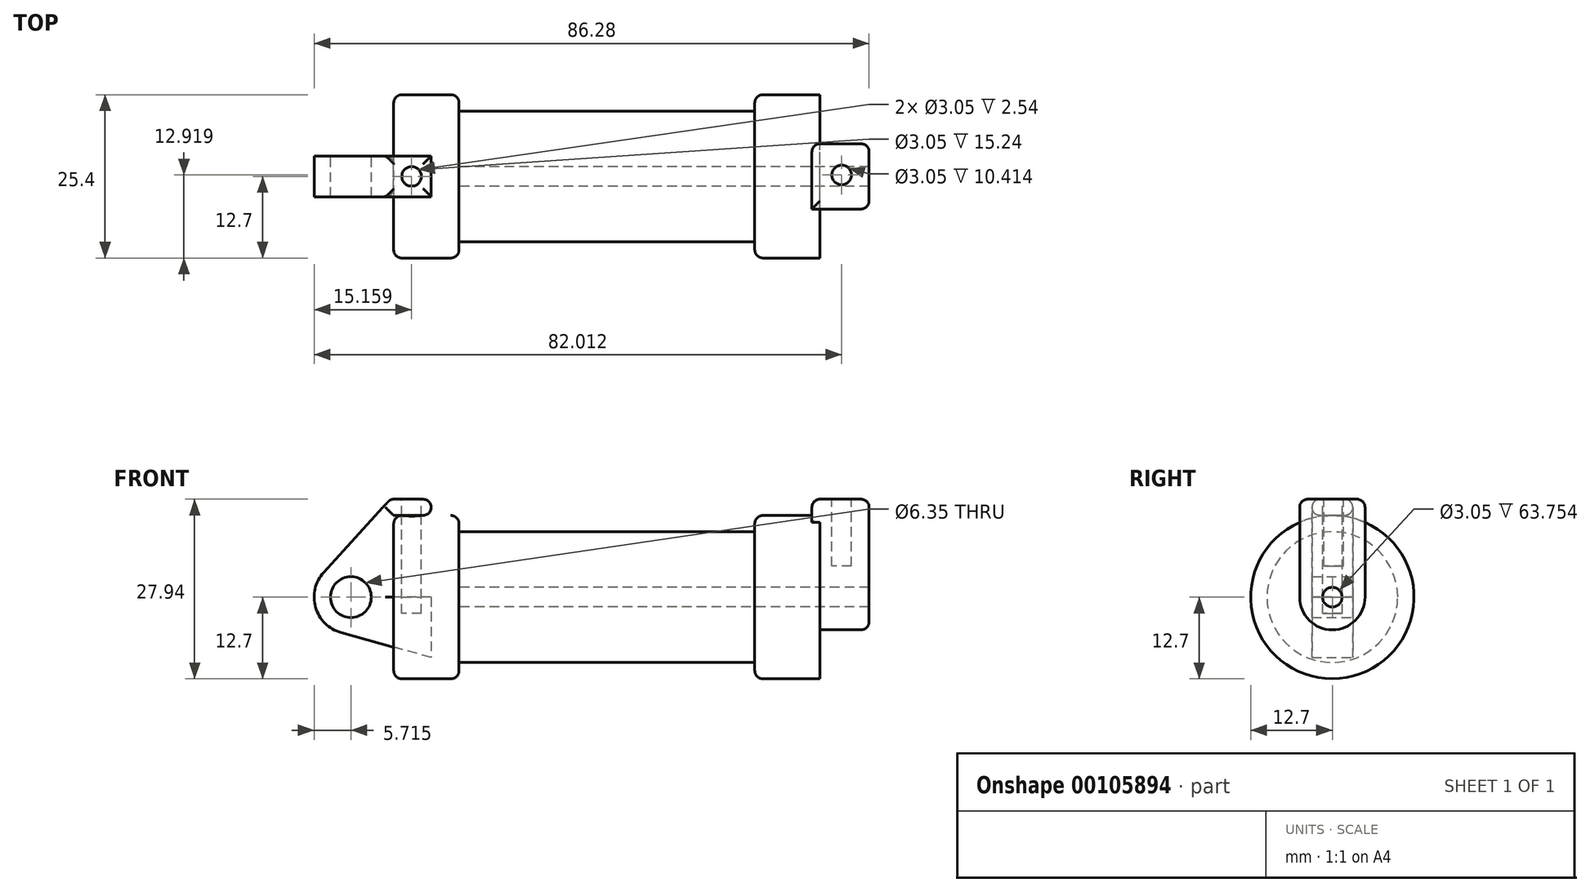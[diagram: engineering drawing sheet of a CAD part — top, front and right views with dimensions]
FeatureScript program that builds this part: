
annotation { "Feature Type Name" : "Feature", "Feature Type Description" : "" }
export const myFeature = defineFeature(function(context is Context, id is Id, definition is map)
    precondition{}
    {
        {
            var Q0;
            Q0=qCreatedBy(makeId("Front.planeOp"),FACE);
            var sketch = newSketch(context, id + "F0", { "sketchPlane" : qUnion([Q0])});
            skLineSegment(sketch, "E0", {"start": v(0, 0) * mm, "end": v(0, 12.7) * mm});
            skLineSegment(sketch, "E1", {"start": v(0, 12.7) * mm, "end": v(10.16, 12.7) * mm});
            skLineSegment(sketch, "E2", {"start": v(10.16, 12.7) * mm, "end": v(10.16, 10.16) * mm});
            skLineSegment(sketch, "E3", {"start": v(10.16, 10.16) * mm, "end": v(56.13, 10.16) * mm});
            skLineSegment(sketch, "E4", {"start": v(56.13, 10.16) * mm, "end": v(56.13, 12.7) * mm});
            skLineSegment(sketch, "E5", {"start": v(56.13, 12.7) * mm, "end": v(66.3, 12.7) * mm});
            skLineSegment(sketch, "E6", {"start": v(66.3, 12.7) * mm, "end": v(66.3, 0) * mm});
            skLineSegment(sketch, "E7", {"start": v(66.3, 0) * mm, "end": v(0, 0) * mm});
            skLineSegment(sketch, "E8", {"start": v(5.84, 15.24) * mm, "end": v(-0.5, 15.24) * mm});
            skLineSegment(sketch, "E9", {"start": v(-0.5, 15.24) * mm, "end": v(-10.88, 3.85) * mm});
            skLineSegment(sketch, "E10", {"start": v(0, 0) * mm, "end": v(-6.65, 0) * mm});
            skCircle(sketch, "E11", {"center": v(-6.65, 0) * mm, "radius": 5.72 * mm});
            skCircle(sketch, "E12", {"center": v(-6.65, 0) * mm, "radius": 3.18 * mm});
            skLineSegment(sketch, "E13", {"start": v(5.84, 15.24) * mm, "end": v(5.84, -9.4) * mm});
            skLineSegment(sketch, "E14", {"start": v(5.84, -9.4) * mm, "end": v(-8.18, -5.5) * mm});
            skSolve(sketch);
        }
        {
            var Q0;
            {var subQ0=sQuery(id+"F0.wireOp",EDGE,"E2");Q0=makeQuery(id+"F0.imprint","IMPRINT",FACE,{"disambiguationData":[TD([[makeQuery(id+"F0.imprint","IMPRINT",EDGE,{"derivedFrom":subQ0}),-1.0]])]});}
            var Q1;
            {var subQ0=sQuery(id+"F0.wireOp",EDGE,"E0");Q1=makeQuery(id+"F0.imprint","IMPRINT",FACE,{"disambiguationData":[TD([[makeQuery(id+"F0.imprint","IMPRINT",EDGE,{"derivedFrom":subQ0}),-1.0]])]});}
            var Q2;
            Q2=sQuery(id+"F0.wireOp",EDGE,"E7");
            revolve(context, id + "F1", {"entities" : qUnion([Q0, Q1]), "axis" : qUnion([Q2]), "revolveType" : RevolveType.FULL});
        }
        {
            var Q0;
            Q0=makeQuery(id+"F1.opRevolve","SWEPT_FACE",FACE,{"disambiguationData":[OSD([sQuery(id+"F0.wireOp",EDGE,"E6")])]});
            var sketch = newSketch(context, id + "F2", { "sketchPlane" : qUnion([Q0])});
            skCircle(sketch, "E15", {"center": v(0, 0) * mm, "radius": 5.08 * mm});
            skCircle(sketch, "E16", {"center": v(0, 0) * mm, "radius": 1.52 * mm});
            skLineSegment(sketch, "E17", {"start": v(-5.08, 0) * mm, "end": v(-5.08, 15.24) * mm});
            skLineSegment(sketch, "E18", {"start": v(5.08, 0) * mm, "end": v(5.08, 15.24) * mm});
            skLineSegment(sketch, "E19", {"start": v(-5.08, 15.24) * mm, "end": v(5.08, 15.24) * mm});
            skLineSegment(sketch, "E20", {"start": v(-2.03, 12.54) * mm, "end": v(-2.03, 15.24) * mm});
            skLineSegment(sketch, "E21", {"start": v(-2.03, 15.24) * mm, "end": v(2.07, 15.24) * mm});
            skLineSegment(sketch, "E22", {"start": v(2.07, 15.24) * mm, "end": v(2.07, 12.53) * mm});
            skSolve(sketch);
        }
        {
            var Q0;
            {var subQ4=sQuery(id+"F0.wireOp",EDGE,"E12");Q0=makeQuery(id+"F0.imprint","IMPRINT",FACE,{"disambiguationData":[TD([[makeQuery(id+"F0.imprint","IMPRINT",EDGE,{"derivedFrom":subQ4}),-1.0]])]});}
            var Q1;
            {var subQ0=sQuery(id+"F0.wireOp",EDGE,"E14");Q1=makeQuery(id+"F0.imprint","IMPRINT",FACE,{"disambiguationData":[TD([[makeQuery(id+"F0.imprint","IMPRINT",EDGE,{"derivedFrom":subQ0}),-1.0]])]});}
            var Q2;
            {var subQ3=sQuery(id+"F0.wireOp",EDGE,"E0");Q2=makeQuery(id+"F0.imprint","IMPRINT",FACE,{"disambiguationData":[TD([[makeQuery(id+"F0.imprint","IMPRINT",EDGE,{"derivedFrom":subQ3}),1.0]])]});}
            extrude(context, id + "F3", {"entities" : qUnion([Q0, Q1, Q2]), "endBound" : BoundingType.SYMMETRIC, "depth" : 6.35 * mm});
        }
        {
            var Q0;
            Q0 = qSketchRegion(id + "F2", true);
            extrude(context, id + "F4", {"entities" : qUnion([Q0]), "operationType" : NewBodyOperationType.ADD, "depth" : 7.62 * mm});
        }
        {
            var Q0;
            Q0=makeQuery(id+"F4.opExtrude","CAP_FACE",FACE,{"disambiguationData":[OSD([sQuery(id+"F2.wireOp",EDGE,"E15"),sQuery(id+"F2.wireOp",EDGE,"E16"),sQuery(id+"F2.wireOp",EDGE,"E17"),sQuery(id+"F2.wireOp",EDGE,"E18"),sQuery(id+"F2.wireOp",EDGE,"E19"),sQuery(id+"F2.wireOp",EDGE,"E21")])],"isStart":true});
            extrude(context, id + "F5", {"entities" : qUnion([Q0]), "operationType" : NewBodyOperationType.ADD, "depth" : 1.27 * mm});
        }
        {
            var Q0;
            Q0=makeQuery(id+"F4.boolean.opBoolean","SPLIT",FACE,{"disambiguationData":[TD([makeQuery(id+"F4.opExtrude","SWEPT_FACE",FACE,{"disambiguationData":[OSD([sQuery(id+"F2.wireOp",EDGE,"E16")])]})])],"derivedFrom":makeQuery(id+"F1.opRevolve","SWEPT_FACE",FACE,{"disambiguationData":[OSD([sQuery(id+"F0.wireOp",EDGE,"E6")])]})});
            var Q1;
            Q1=makeQuery(id+"F1.opRevolve","SWEPT_FACE",FACE,{"disambiguationData":[OSD([sQuery(id+"F0.wireOp",EDGE,"E2")])]});
            extrude(context, id + "F6", {"entities" : qUnion([Q0]), "operationType" : NewBodyOperationType.REMOVE, "endBound" : BoundingType.UP_TO_SURFACE, "oppositeDirection" : true, "endBoundEntityFace" : qUnion([Q1]), "depth" : 25.4 * mm});
        }
        {
            var Q0;
            {var subQ0=sQuery(id+"F2.wireOp",EDGE,"E21");var subQ1=sQuery(id+"F2.wireOp",EDGE,"E19");Q0=makeQuery(id+"F5.boolean.opBoolean","MERGE",FACE,{"derivedFrom":[makeQuery(id+"F4.opExtrude","SWEPT_FACE",FACE,{"disambiguationData":[OSD([subQ1,subQ0])]}),makeQuery(id+"F5.opExtrude","SWEPT_FACE",FACE,{"disambiguationData":[OSD([subQ1,subQ0])]})]});}
            var sketch = newSketch(context, id + "F7", { "sketchPlane" : qUnion([Q0])});
            skCircle(sketch, "E23", {"center": v(69.64, 0.22) * mm, "radius": 1.52 * mm});
            skCircle(sketch, "E24", {"center": v(2.79, 0) * mm, "radius": 1.52 * mm});
            skSolve(sketch);
        }
        {
            var Q0;
            Q0=makeQuery(id+"F7.imprint","IMPRINT",FACE,{"disambiguationData":[TD([[makeQuery(id+"F7.imprint","IMPRINT",EDGE,{"derivedFrom":sQuery(id+"F7.wireOp",EDGE,"E24")}),1.0]])]});
            extrude(context, id + "F8", {"entities" : qUnion([Q0]), "operationType" : NewBodyOperationType.REMOVE, "oppositeDirection" : true, "depth" : 17.78 * mm});
        }
        {
            var Q0;
            Q0 = qSketchRegion(id + "F7", true);
            var Q1;
            Q1=makeQuery(id+"F4.opExtrude","SWEPT_FACE",FACE,{"disambiguationData":[OSD([sQuery(id+"F2.wireOp",EDGE,"E15")])]});
            extrude(context, id + "F9", {"entities" : qUnion([Q0]), "operationType" : NewBodyOperationType.REMOVE, "oppositeDirection" : true, "endBoundEntityFace" : qUnion([Q1]), "depth" : 10.4 * mm});
        }
        {
            var Q0;
            Q0=makeQuery(id+"F7.imprint","IMPRINT",FACE,{"disambiguationData":[TD([[makeQuery(id+"F7.imprint","IMPRINT",EDGE,{"derivedFrom":sQuery(id+"F7.wireOp",EDGE,"E23")}),1.0]])]});
            extrude(context, id + "F10", {"entities" : qUnion([Q0]), "operationType" : NewBodyOperationType.REMOVE, "oppositeDirection" : true, "depth" : 10.4 * mm});
        }
        {
            var Q0;
            {var subQ0=sQuery(id+"F2.wireOp",EDGE,"E19");var subQ1=sQuery(id+"F2.wireOp",EDGE,"E18");Q0=makeQuery(id+"F5.boolean.opBoolean","MERGE",EDGE,{"derivedFrom":[makeQuery(id+"F4.opExtrude","SWEPT_EDGE",EDGE,{"disambiguationData":[OSD([subQ1,subQ0])]}),makeQuery(id+"F5.opExtrude","SWEPT_EDGE",EDGE,{"disambiguationData":[OSD([subQ1,subQ0])]})]});}
            var Q1;
            Q1=makeQuery(id+"F5.opExtrude","CAP_EDGE",EDGE,{"disambiguationData":[OSD([sQuery(id+"F2.wireOp",EDGE,"E19"),sQuery(id+"F2.wireOp",EDGE,"E21")])],"isStart":false});
            var Q2;
            Q2=makeQuery(id+"F5.opExtrude","CAP_EDGE",EDGE,{"disambiguationData":[OSD([sQuery(id+"F2.wireOp",EDGE,"E18")])],"isStart":false});
            var Q3;
            Q3=makeQuery(id+"F5.opExtrude","CAP_EDGE",EDGE,{"disambiguationData":[OSD([sQuery(id+"F0.wireOp",EDGE,"E5"),sQuery(id+"F0.wireOp",EDGE,"E6")])],"isStart":false});
            var Q4;
            Q4=makeQuery(id+"F4.opExtrude","CAP_EDGE",EDGE,{"disambiguationData":[OSD([sQuery(id+"F2.wireOp",EDGE,"E18")])],"isStart":false});
            var Q5;
            Q5=makeQuery(id+"F4.opExtrude","CAP_EDGE",EDGE,{"disambiguationData":[OSD([sQuery(id+"F2.wireOp",EDGE,"E19"),sQuery(id+"F2.wireOp",EDGE,"E21")])],"isStart":false});
            var Q6;
            {var subQ0=sQuery(id+"F2.wireOp",EDGE,"E19");var subQ1=sQuery(id+"F2.wireOp",EDGE,"E17");Q6=makeQuery(id+"F5.boolean.opBoolean","MERGE",EDGE,{"derivedFrom":[makeQuery(id+"F4.opExtrude","SWEPT_EDGE",EDGE,{"disambiguationData":[OSD([subQ1,subQ0])]}),makeQuery(id+"F5.opExtrude","SWEPT_EDGE",EDGE,{"disambiguationData":[OSD([subQ1,subQ0])]})]});}
            var Q7;
            Q7=makeQuery(id+"F3.opExtrude","CAP_EDGE",EDGE,{"disambiguationData":[OSD([sQuery(id+"F0.wireOp",EDGE,"E0")])],"isStart":true});
            var Q8;
            Q8=makeQuery(id+"F3.opExtrude","CAP_EDGE",EDGE,{"disambiguationData":[OSD([sQuery(id+"F0.wireOp",EDGE,"E1")])],"isStart":true});
            var Q9;
            Q9=makeQuery(id+"F3.opExtrude","CAP_EDGE",EDGE,{"disambiguationData":[OSD([sQuery(id+"F0.wireOp",EDGE,"E0")])],"isStart":false});
            var Q10;
            Q10=makeQuery(id+"F3.opExtrude","CAP_EDGE",EDGE,{"disambiguationData":[OSD([sQuery(id+"F0.wireOp",EDGE,"E1")])],"isStart":false});
            var Q11;
            Q11=makeQuery(id+"F1.opRevolve","SWEPT_EDGE",EDGE,{"disambiguationData":[OSD([sQuery(id+"F0.wireOp",EDGE,"E1"),sQuery(id+"F0.wireOp",EDGE,"E2")])]});
            var Q12;
            Q12=makeQuery(id+"F1.opRevolve","SWEPT_EDGE",EDGE,{"disambiguationData":[OSD([sQuery(id+"F0.wireOp",EDGE,"E0"),sQuery(id+"F0.wireOp",EDGE,"E1")])]});
            var Q13;
            Q13=makeQuery(id+"F1.opRevolve","SWEPT_EDGE",EDGE,{"disambiguationData":[OSD([sQuery(id+"F0.wireOp",EDGE,"E4"),sQuery(id+"F0.wireOp",EDGE,"E5")])]});
            var Q14;
            Q14=makeQuery(id+"F4.opExtrude","CAP_EDGE",EDGE,{"disambiguationData":[OSD([sQuery(id+"F2.wireOp",EDGE,"E17")])],"isStart":false});
            var Q15;
            Q15=makeQuery(id+"F3.opExtrude","CAP_EDGE",EDGE,{"disambiguationData":[OSD([sQuery(id+"F0.wireOp",EDGE,"E8")])],"isStart":false});
            var Q16;
            Q16=makeQuery(id+"F3.opExtrude","SWEPT_EDGE",EDGE,{"disambiguationData":[OSD([sQuery(id+"F0.wireOp",EDGE,"E8"),sQuery(id+"F0.wireOp",EDGE,"E9")])]});
            var Q17;
            Q17=makeQuery(id+"F3.opExtrude","CAP_EDGE",EDGE,{"disambiguationData":[OSD([sQuery(id+"F0.wireOp",EDGE,"E8")])],"isStart":true});
            var Q18;
            Q18=makeQuery(id+"F3.opExtrude","SWEPT_EDGE",EDGE,{"disambiguationData":[OSD([sQuery(id+"F0.wireOp",EDGE,"E8"),sQuery(id+"F0.wireOp",EDGE,"E13")])]});
            var Q19;
            Q19=makeQuery(id+"F3.opExtrude","SWEPT_EDGE",EDGE,{"disambiguationData":[OSD([sQuery(id+"F0.wireOp",EDGE,"E1"),sQuery(id+"F0.wireOp",EDGE,"E13")])]});
            fillet(context, id + "F11", {"entities" : qUnion([Q0, Q1, Q2, Q3, Q4, Q5, Q6, Q7, Q8, Q9, Q10, Q11, Q12, Q13, Q14, Q15, Q16, Q17, Q18, Q19]), "radius" : 1.27 * mm, "tangentPropagation" : true, "allowEdgeOverflow" : false});
        }
    });
